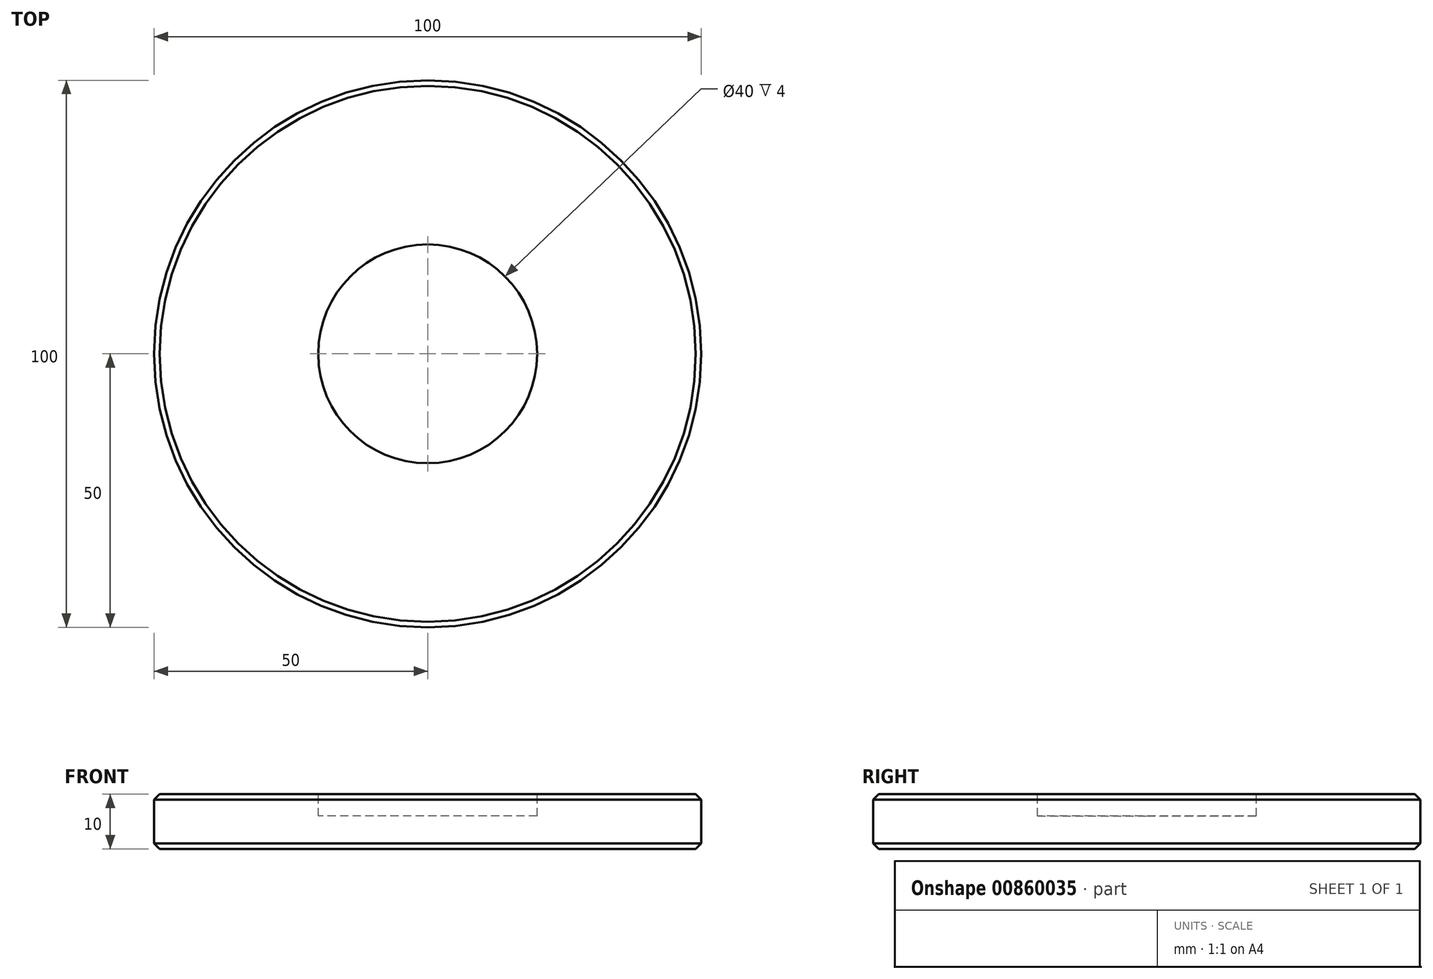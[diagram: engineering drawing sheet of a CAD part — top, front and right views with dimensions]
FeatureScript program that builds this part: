
annotation { "Feature Type Name" : "Feature", "Feature Type Description" : "" }
export const myFeature = defineFeature(function(context is Context, id is Id, definition is map)
    precondition{}
    {
        {
            var Q0;
            Q0=qCreatedBy(makeId("Top.planeOp"),FACE);
            var sketch = newSketch(context, id + "F0", { "sketchPlane" : qUnion([Q0])});
            skCircle(sketch, "E0", {"center": v(0, 0) * mm, "radius": 50 * mm});
            skSolve(sketch);
        }
        {
            var Q0;
            Q0=makeQuery(id+"F0.imprint","IMPRINT",FACE,{"disambiguationData":[TD([[makeQuery(id+"F0.imprint","IMPRINT",EDGE,{"derivedFrom":sQuery(id+"F0.wireOp",EDGE,"E0")}),1.0]])]});
            extrude(context, id + "F1", {"entities" : qUnion([Q0]), "depth" : 10 * mm, "offsetDistance" : 25 * mm});
        }
        {
            var Q0;
            Q0=makeQuery(id+"F1.opExtrude","CAP_FACE",FACE,{"disambiguationData":[OSD([sQuery(id+"F0.wireOp",EDGE,"E0")])],"isStart":false});
            var sketch = newSketch(context, id + "F2", { "sketchPlane" : qUnion([Q0])});
            skCircle(sketch, "E1", {"center": v(0, 0) * mm, "radius": 20 * mm});
            skSolve(sketch);
        }
        {
            var Q0;
            Q0 = qSketchRegion(id + "F2", true);
            extrude(context, id + "F3", {"entities" : qUnion([Q0]), "operationType" : NewBodyOperationType.REMOVE, "oppositeDirection" : true, "depth" : 4 * mm, "offsetDistance" : 25 * mm});
        }
        {
            var Q0;
            Q0=makeQuery(id+"F1.opExtrude","CAP_EDGE",EDGE,{"disambiguationData":[OSD([sQuery(id+"F0.wireOp",EDGE,"E0")])],"isStart":false});
            var Q1;
            Q1=makeQuery(id+"F1.opExtrude","CAP_EDGE",EDGE,{"disambiguationData":[OSD([sQuery(id+"F0.wireOp",EDGE,"E0")])],"isStart":true});
            chamfer(context, id + "F4", {"entities" : qUnion([Q0, Q1]), "width" : 1 * mm, "tangentPropagation" : true});
        }
    });
